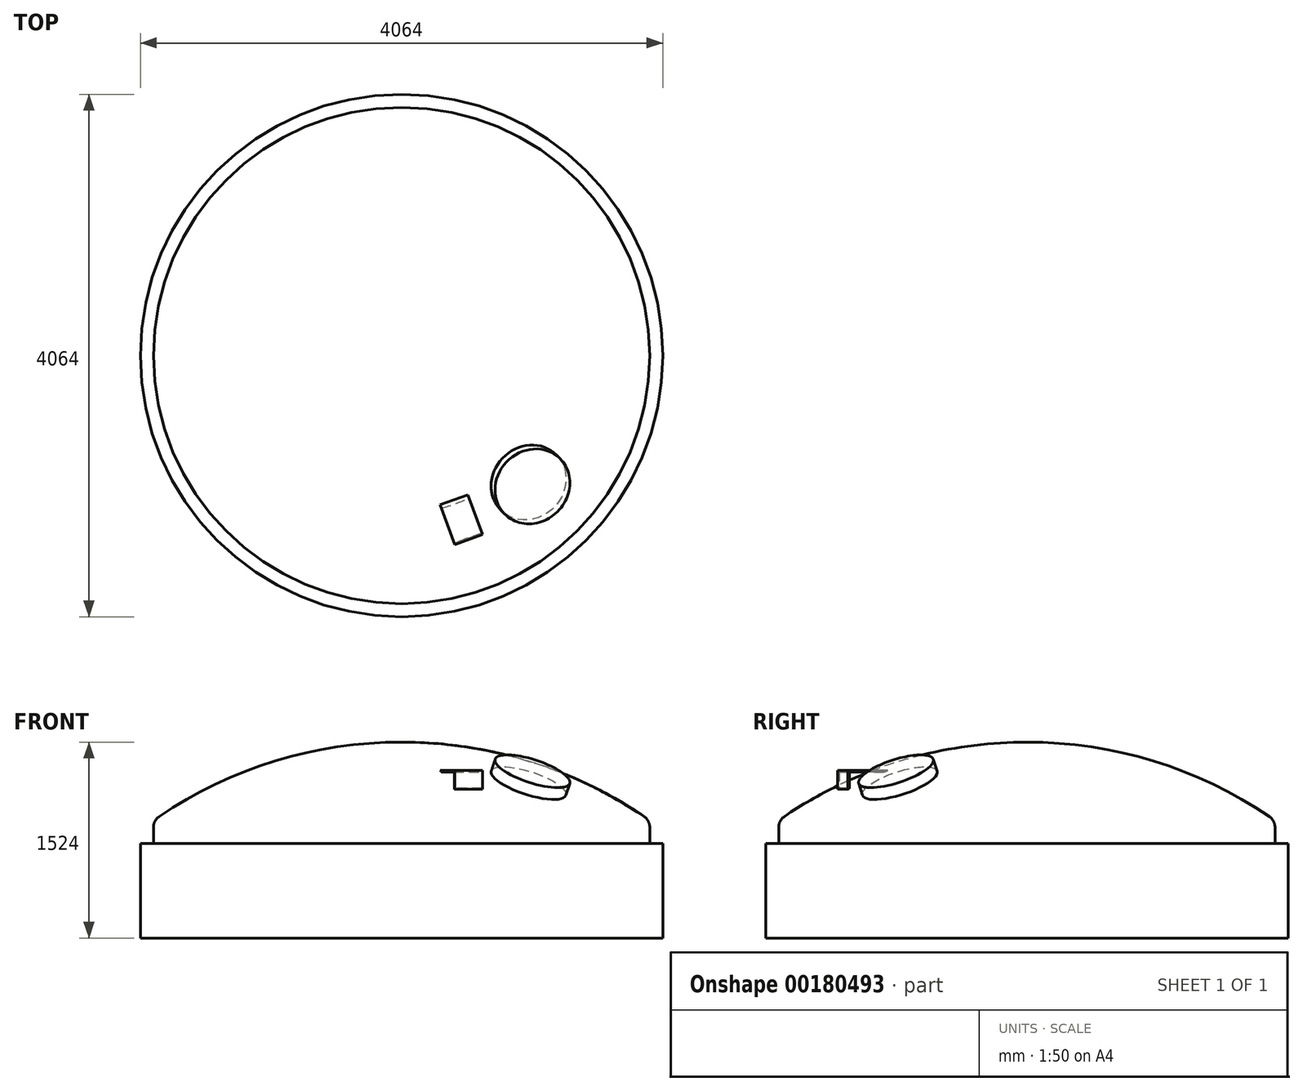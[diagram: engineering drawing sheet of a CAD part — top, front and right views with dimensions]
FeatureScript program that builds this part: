
annotation { "Feature Type Name" : "Feature", "Feature Type Description" : "" }
export const myFeature = defineFeature(function(context is Context, id is Id, definition is map)
    precondition{}
    {
        {
            var Q0;
            Q0=qCreatedBy(makeId("Front.planeOp"),FACE);
            var sketch = newSketch(context, id + "F0", { "sketchPlane" : qUnion([Q0])});
            skLineSegment(sketch, "E0", {"start": v(0, 0) * mm, "end": v(0, 1843.9) * mm, "construction": true});
            skLineSegment(sketch, "E1", {"start": v(0, 1524) * mm, "end": v(264.22, 1524) * mm, "construction": true});
            skArc(sketch, "E2", {"start": v(1885.8, 945.15) * mm, "mid": v(986.32, 1376.03) * mm, "end": v(0, 1524) * mm});
            skLineSegment(sketch, "E3", {"start": v(1930.4, 861.05) * mm, "end": v(1930.4, 736.6) * mm});
            skLineSegment(sketch, "E4", {"start": v(1930.4, 736.6) * mm, "end": v(2032, 736.6) * mm});
            skLineSegment(sketch, "E5", {"start": v(2032, 736.6) * mm, "end": v(2032, 0) * mm});
            skLineSegment(sketch, "E6", {"start": v(2032, 0) * mm, "end": v(0, 0) * mm});
            skPoint(sketch, "E7.visualSharp", {"position": v(1930.4, 914.4) * mm});
            skArc(sketch, "E7.filletArc", {"start": v(1930.4, 861.05) * mm, "mid": v(1918.56, 908.65) * mm, "end": v(1885.8, 945.15) * mm});
            skLineSegment(sketch, "E8", {"start": v(0, 1524) * mm, "end": v(0, 0) * mm});
            skSolve(sketch);
        }
        {
            var Q0;
            Q0 = qSketchRegion(id + "F0", true);
            var Q1;
            Q1=sQuery(id+"F0.wireOp",EDGE,"E0");
            revolve(context, id + "F1", {"entities" : qUnion([Q0]), "axis" : qUnion([Q1]), "revolveType" : RevolveType.FULL});
        }
        {
            var Q0;
            Q0=sQuery(id+"F0.wireOp",EDGE,"E0");
            var Q1;
            Q1=qCreatedBy(makeId("Front.planeOp"),FACE);
            cPlane(context, id + "F2", {"entities" : qUnion([Q0, Q1]), "cplaneType" : CPlaneType.LINE_ANGLE, "offset" : 25.4 * mm, "angle" : 135 * degree, "width" : 152.4 * mm, "height" : 152.4 * mm});
        }
        {
            var Q0;
            Q0=qCreatedBy(id+"F2.planeOp",FACE);
            var sketch = newSketch(context, id + "F3", { "sketchPlane" : qUnion([Q0])});
            skArc(sketch, "E9", {"start": v(1885.8, 945.15) * mm, "mid": v(0, 1524) * mm, "end": v(-1885.8, 945.15) * mm, "construction": true});
            skLineSegment(sketch, "E10", {"start": v(1402.78, 1217.3) * mm, "end": v(1539.62, 1515.26) * mm, "construction": true});
            skLineSegment(sketch, "E11", {"start": v(1120.01, 1331.91) * mm, "end": v(1162.41, 1424.24) * mm});
            skLineSegment(sketch, "E12", {"start": v(1120.01, 1331.91) * mm, "end": v(1397, 1204.7) * mm});
            skLineSegment(sketch, "E13", {"start": v(1397, 1204.7) * mm, "end": v(1461.98, 1346.2) * mm});
            skArc(sketch, "E14", {"start": v(1461.98, 1346.2) * mm, "mid": v(1315.63, 1398.4) * mm, "end": v(1162.41, 1424.24) * mm});
            skLineSegment(sketch, "E15", {"start": v(1397, 1204.7) * mm, "end": v(1673.99, 1077.5) * mm, "construction": true});
            skLineSegment(sketch, "E16", {"start": v(1461.98, 1346.2) * mm, "end": v(1310.1, 1415.95) * mm, "construction": true});
            skSolve(sketch);
        }
        {
            var Q0;
            Q0=makeQuery(id+"F3.imprint","IMPRINT",FACE,{"disambiguationData":[TD([[makeQuery(id+"F3.imprint","IMPRINT",EDGE,{"derivedFrom":sQuery(id+"F3.wireOp",EDGE,"E11")}),-1.0]])]});
            var Q1;
            Q1=sQuery(id+"F3.wireOp",EDGE,"E10");
            revolve(context, id + "F4", {"operationType" : NewBodyOperationType.ADD, "entities" : qUnion([Q0]), "axis" : qUnion([Q1]), "revolveType" : RevolveType.FULL});
        }
        {
            var Q0;
            Q0=qCreatedBy(makeId("Front.planeOp"),FACE);
            var Q1;
            Q1=sQuery(id+"F0.wireOp",EDGE,"E0");
            cPlane(context, id + "F5", {"entities" : qUnion([Q0, Q1]), "cplaneType" : CPlaneType.LINE_ANGLE, "offset" : 25.4 * mm, "angle" : 110 * degree, "width" : 152.4 * mm, "height" : 152.4 * mm});
        }
        {
            var Q0;
            Q0=qCreatedBy(id+"F5.planeOp",FACE);
            var sketch = newSketch(context, id + "F6", { "sketchPlane" : qUnion([Q0])});
            skLineSegment(sketch, "E17.bottom", {"start": v(1193.8, 1304.86) * mm, "end": v(1524, 1304.86) * mm});
            skLineSegment(sketch, "E17.top", {"start": v(1193.8, 1292.16) * mm, "end": v(1511.3, 1292.16) * mm});
            skLineSegment(sketch, "E17.left", {"start": v(1193.8, 1304.86) * mm, "end": v(1193.8, 1292.16) * mm});
            skLineSegment(sketch, "E18.top", {"start": v(1524, 1158.65) * mm, "end": v(1511.3, 1158.65) * mm});
            skLineSegment(sketch, "E18.right", {"start": v(1511.3, 1292.16) * mm, "end": v(1511.3, 1158.65) * mm});
            skLineSegment(sketch, "E19", {"start": v(1524, 1304.86) * mm, "end": v(1524, 1158.65) * mm});
            skArc(sketch, "E20", {"start": v(1885.8, 945.15) * mm, "mid": v(0, 1524) * mm, "end": v(-1885.8, 945.15) * mm, "construction": true});
            skSolve(sketch);
        }
        {
            var Q0;
            Q0 = qSketchRegion(id + "F6", true);
            extrude(context, id + "F7", {"entities" : qUnion([Q0]), "operationType" : NewBodyOperationType.ADD, "endBound" : BoundingType.SYMMETRIC, "depth" : 228.6 * mm});
        }
    });
